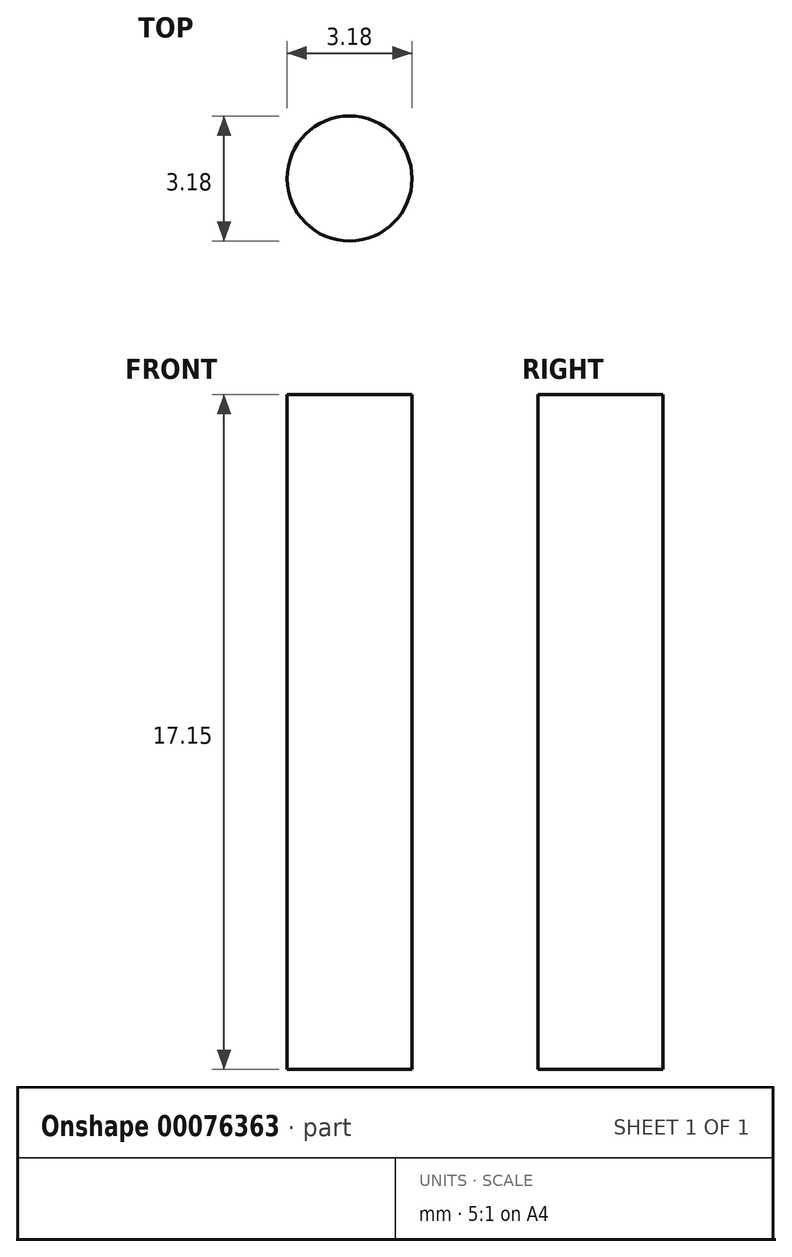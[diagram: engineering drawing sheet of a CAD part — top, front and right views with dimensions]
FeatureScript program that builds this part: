
annotation { "Feature Type Name" : "Feature", "Feature Type Description" : "" }
export const myFeature = defineFeature(function(context is Context, id is Id, definition is map)
    precondition{}
    {
        {
            var Q0;
            Q0=qCreatedBy(makeId("Front.planeOp"),FACE);
            var sketch = newSketch(context, id + "F0", { "sketchPlane" : qUnion([Q0])});
            skLineSegment(sketch, "E0.left", {"start": v(0, 0) * mm, "end": v(0, 22.92) * mm});
            skArc(sketch, "E1", {"start": v(0, 51.45) * mm, "mid": v(-0.04, 50.17) * mm, "end": v(0, 48.89) * mm});
            skLineSegment(sketch, "E2", {"start": v(0, 51.45) * mm, "end": v(0, 22.92) * mm});
            skLineSegment(sketch, "E3", {"start": v(1.59, 0) * mm, "end": v(0, 0) * mm});
            skLineSegment(sketch, "E4.top", {"start": v(1.59, 17.15) * mm, "end": v(0, 17.15) * mm});
            skLineSegment(sketch, "E4.right", {"start": v(0, 0) * mm, "end": v(0, 17.15) * mm});
            skLineSegment(sketch, "E5", {"start": v(1.59, 17.15) * mm, "end": v(1.59, 0) * mm});
            skArc(sketch, "E6", {"start": v(1.59, 0) * mm, "mid": v(14.94, 13.42) * mm, "end": v(22.88, 30.62) * mm});
            skLineSegment(sketch, "E7.bottom", {"start": v(0, 51.45) * mm, "end": v(4.76, 51.45) * mm});
            skLineSegment(sketch, "E7.top", {"start": v(0, 47) * mm, "end": v(4.76, 47) * mm});
            skLineSegment(sketch, "E7.left", {"start": v(0, 51.45) * mm, "end": v(0, 47) * mm});
            skLineSegment(sketch, "E7.right", {"start": v(4.76, 51.45) * mm, "end": v(4.76, 47) * mm});
            skFitSpline(sketch, "E8", {"points": [v(4.76, 51.45) * mm, v(14.07, 46.88) * mm, v(20.18, 47.1) * mm, v(22.88, 30.62) * mm], "startDerivative": vector(28.5, -20.46) * mm, "endDerivative": vector(1, -53.57) * mm});
            skSolve(sketch);
        }
        {
            var Q0;
            {var subQ1=sQuery(id+"F0.wireOp",EDGE,"E0.left");Q0=makeQuery(id+"F0.imprint","IMPRINT",FACE,{"disambiguationData":[TD([[makeQuery(id+"F0.imprint","IMPRINT",EDGE,{"derivedFrom":subQ1}),-1.0]])]});}
            var Q1;
            Q1=sQuery(id+"F0.wireOp",EDGE,"E0.left");
            revolve(context, id + "F1", {"entities" : qUnion([Q0]), "axis" : qUnion([Q1]), "revolveType" : RevolveType.FULL});
        }
    });
